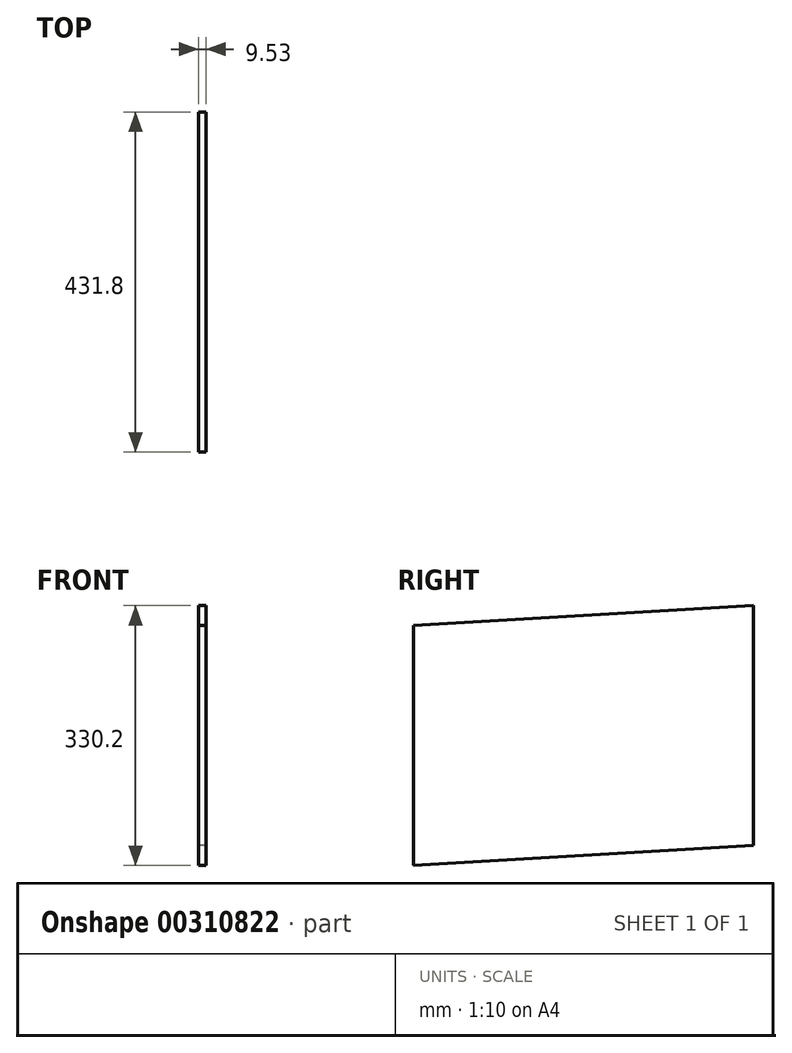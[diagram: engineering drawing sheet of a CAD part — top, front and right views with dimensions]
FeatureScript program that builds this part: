
annotation { "Feature Type Name" : "Feature", "Feature Type Description" : "" }
export const myFeature = defineFeature(function(context is Context, id is Id, definition is map)
    precondition{}
    {
        {
            var Q0;
            Q0=qCreatedBy(makeId("Right.planeOp"),FACE);
            var sketch = newSketch(context, id + "F0", { "sketchPlane" : qUnion([Q0])});
            skLineSegment(sketch, "E0", {"start": v(-603.98, -82.15) * mm, "end": v(-172.18, -56.75) * mm});
            skLineSegment(sketch, "E1", {"start": v(-603.98, 222.65) * mm, "end": v(-172.18, 248.05) * mm});
            skLineSegment(sketch, "E2", {"start": v(-172.18, 248.05) * mm, "end": v(-172.18, -56.75) * mm});
            skLineSegment(sketch, "E3", {"start": v(-603.98, -82.15) * mm, "end": v(-603.98, 222.65) * mm});
            skSolve(sketch);
        }
        {
            var Q0;
            Q0=makeQuery(id+"F0.imprint","IMPRINT",FACE,{"disambiguationData":[TD([[makeQuery(id+"F0.imprint","IMPRINT",EDGE,{"derivedFrom":sQuery(id+"F0.wireOp",EDGE,"E0")}),1.0]])]});
            extrude(context, id + "F1", {"entities" : qUnion([Q0]), "depth" : 9.52 * mm});
        }
        {
            var Q0;
            Q0=makeQuery(id+"F1.opExtrude","SWEPT_BODY",BODY,{"disambiguationData":[OSD([sQuery(id+"F0.wireOp",EDGE,"E0"),sQuery(id+"F0.wireOp",EDGE,"E1"),sQuery(id+"F0.wireOp",EDGE,"E2"),sQuery(id+"F0.wireOp",EDGE,"E3")])]});
            transform(context, id + "F2", {"entities" : qUnion([Q0]), "transformType" : TransformType.TRANSLATION_3D, "dx" : 482.6 * mm, "dy" : 0 * mm, "dz" : 0 * mm, "makeCopy" : true});
        }
        {
            var Q0;
            Q0=makeQuery(id+"F2.opPattern","COPY",BODY,{"derivedFrom":makeQuery(id+"F1.opExtrude","SWEPT_BODY",BODY,{"disambiguationData":[OSD([sQuery(id+"F0.wireOp",EDGE,"E0"),sQuery(id+"F0.wireOp",EDGE,"E1"),sQuery(id+"F0.wireOp",EDGE,"E2"),sQuery(id+"F0.wireOp",EDGE,"E3")])]}),"instanceName":"1"});
            deleteBodies(context, id + "F3", {"entities" : qUnion([Q0])});
        }
    });
